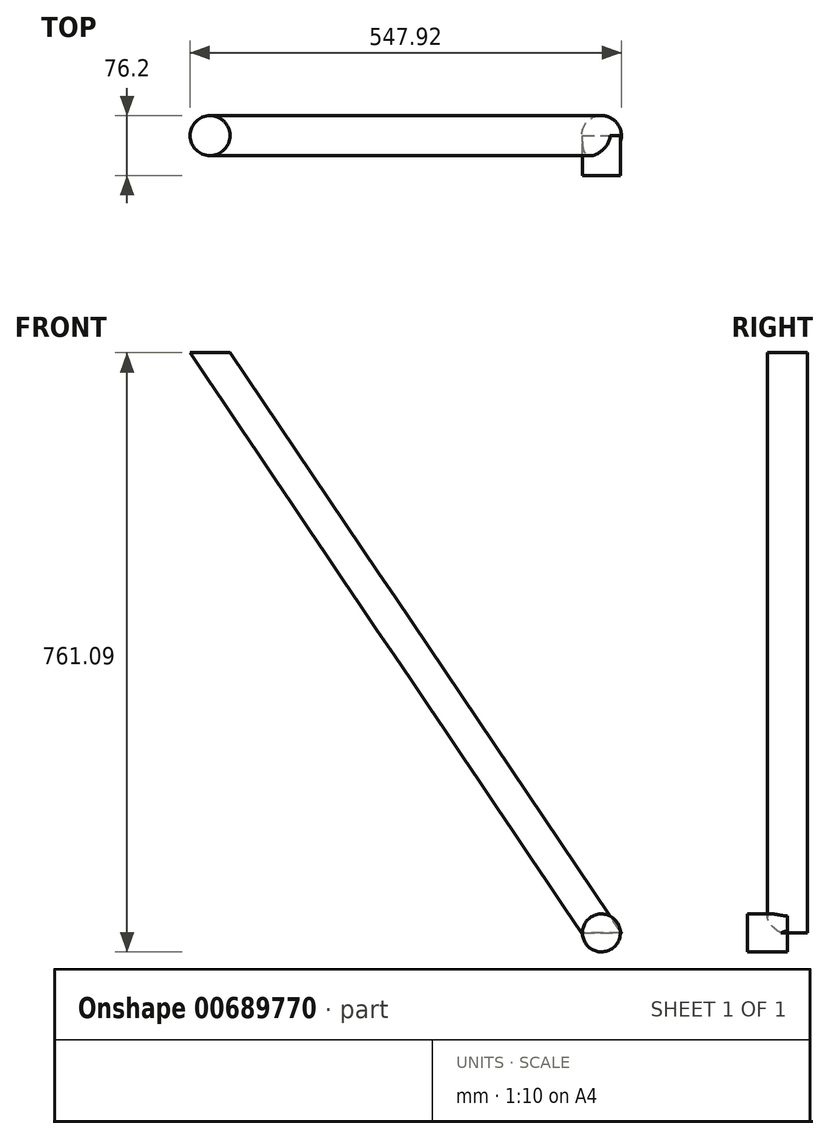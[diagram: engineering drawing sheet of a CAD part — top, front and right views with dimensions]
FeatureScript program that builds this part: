
annotation { "Feature Type Name" : "Feature", "Feature Type Description" : "" }
export const myFeature = defineFeature(function(context is Context, id is Id, definition is map)
    precondition{}
    {
        {
            var Q0;
            Q0=qCreatedBy(makeId("Front.planeOp"),FACE);
            var sketch = newSketch(context, id + "F0", { "sketchPlane" : qUnion([Q0])});
            skLineSegment(sketch, "E0", {"start": v(0, 0) * mm, "end": v(-497.12, 737.01) * mm});
            skSolve(sketch);
        }
        {
            var Q0;
            Q0=qCreatedBy(makeId("Top.planeOp"),FACE);
            var sketch = newSketch(context, id + "F1", { "sketchPlane" : qUnion([Q0])});
            skCircle(sketch, "E1", {"center": v(0, 0) * mm, "radius": 25.4 * mm});
            skSolve(sketch);
        }
        {
            var Q0;
            Q0=makeQuery(id+"F1.imprint","IMPRINT",FACE,{"disambiguationData":[TD([[makeQuery(id+"F1.imprint","IMPRINT",EDGE,{"derivedFrom":sQuery(id+"F1.wireOp",EDGE,"E1")}),1.0]])]});
            var Q1;
            Q1=sQuery(id+"F0.wireOp",EDGE,"E0");
            sweep(context, id + "F2", {"profiles" : qUnion([Q0]), "path" : qUnion([Q1])});
        }
        {
            var Q0;
            Q0=qCreatedBy(makeId("Front.planeOp"),FACE);
            var sketch = newSketch(context, id + "F3", { "sketchPlane" : qUnion([Q0])});
            skCircle(sketch, "E2", {"center": v(0, 0) * mm, "radius": 24.08 * mm});
            skSolve(sketch);
        }
        {
            var Q0;
            Q0=makeQuery(id+"F3.imprint","IMPRINT",FACE,{"disambiguationData":[TD([[makeQuery(id+"F3.imprint","IMPRINT",EDGE,{"derivedFrom":sQuery(id+"F3.wireOp",EDGE,"E2")}),1.0]])]});
            extrude(context, id + "F4", {"entities" : qUnion([Q0]), "operationType" : NewBodyOperationType.ADD, "depth" : 50.8 * mm, "offsetDistance" : 25.4 * mm});
        }
    });
